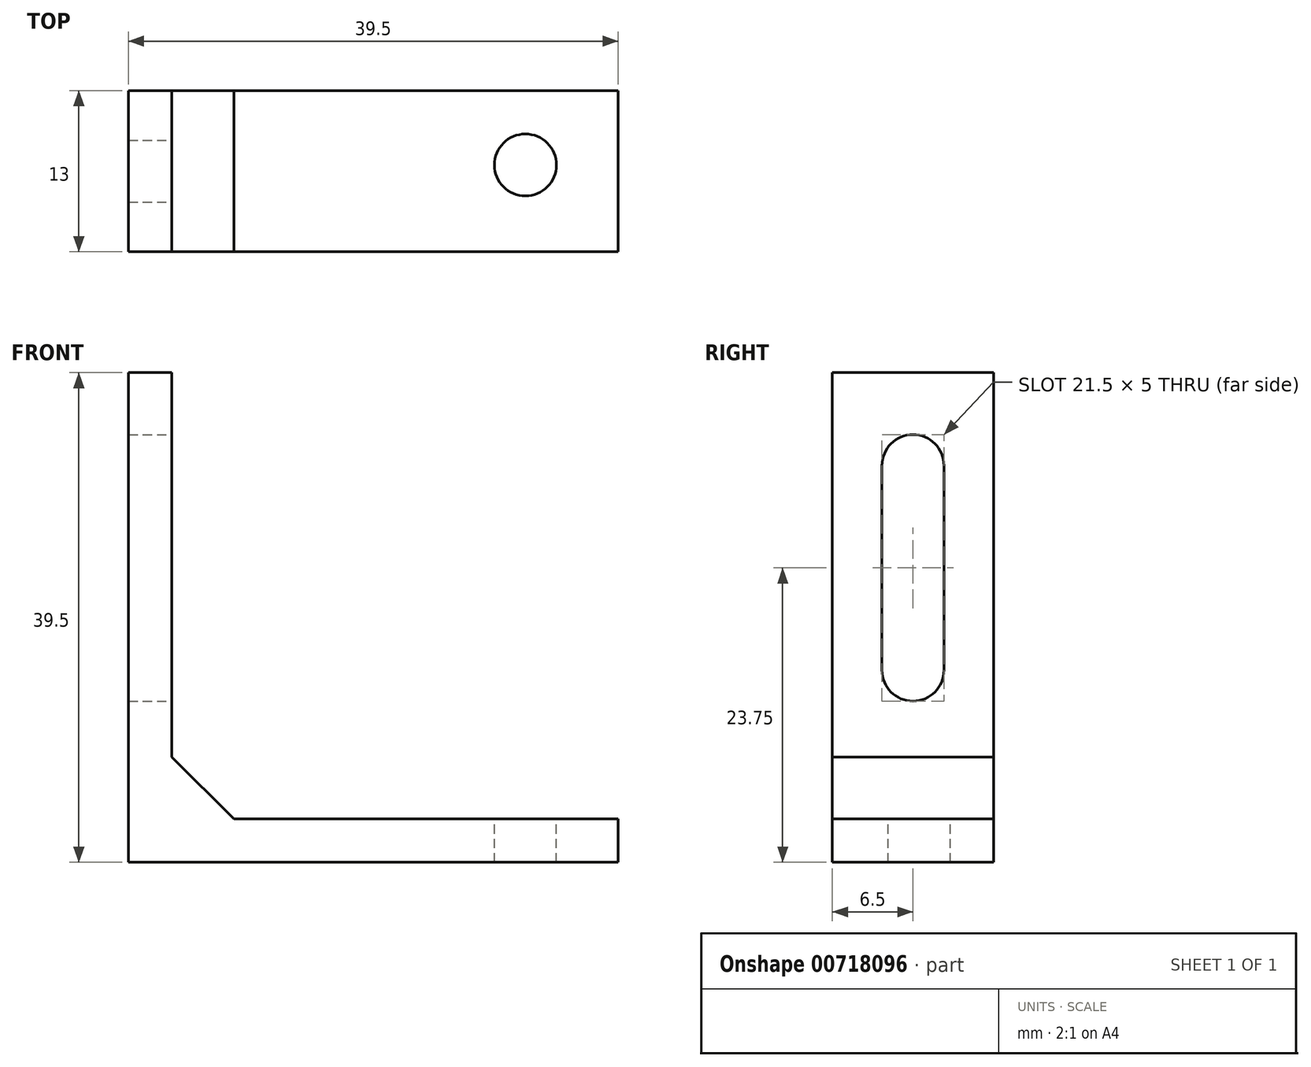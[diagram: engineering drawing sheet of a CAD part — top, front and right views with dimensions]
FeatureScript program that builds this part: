
annotation { "Feature Type Name" : "Feature", "Feature Type Description" : "" }
export const myFeature = defineFeature(function(context is Context, id is Id, definition is map)
    precondition{}
    {
        {
            var Q0;
            Q0=qCreatedBy(makeId("Front.planeOp"),FACE);
            var sketch = newSketch(context, id + "F0", { "sketchPlane" : qUnion([Q0])});
            skLineSegment(sketch, "E0", {"start": v(0, 0) * mm, "end": v(-36, 0) * mm});
            skLineSegment(sketch, "E1", {"start": v(-36, 0) * mm, "end": v(-36, 36) * mm});
            skLineSegment(sketch, "E2", {"start": v(-36, 36) * mm, "end": v(-39.5, 36) * mm});
            skLineSegment(sketch, "E3", {"start": v(-39.5, 36) * mm, "end": v(-39.5, -3.5) * mm});
            skLineSegment(sketch, "E4", {"start": v(-39.5, -3.5) * mm, "end": v(0, -3.5) * mm});
            skLineSegment(sketch, "E5", {"start": v(0, -3.5) * mm, "end": v(0, 0) * mm});
            skSolve(sketch);
        }
        {
            var Q0;
            Q0=makeQuery(id+"F0.imprint","IMPRINT",FACE,{"disambiguationData":[TD([[makeQuery(id+"F0.imprint","IMPRINT",EDGE,{"derivedFrom":sQuery(id+"F0.wireOp",EDGE,"E0")}),1.0]])]});
            extrude(context, id + "F1", {"entities" : qUnion([Q0]), "depth" : 13 * mm, "offsetDistance" : 25 * mm});
        }
        {
            var Q0;
            Q0=makeQuery(id+"F1.opExtrude","SWEPT_FACE",FACE,{"disambiguationData":[OSD([sQuery(id+"F0.wireOp",EDGE,"E1")])]});
            var sketch = newSketch(context, id + "F2", { "sketchPlane" : qUnion([Q0])});
            skCircle(sketch, "E6", {"center": v(-6.5, 28.5) * mm, "radius": 2.5 * mm});
            skCircle(sketch, "E7", {"center": v(-6.5, 12) * mm, "radius": 2.5 * mm});
            skLineSegment(sketch, "E8", {"start": v(-9, 12) * mm, "end": v(-9, 28.5) * mm});
            skLineSegment(sketch, "E9", {"start": v(-4, 28.5) * mm, "end": v(-4, 12) * mm});
            skSolve(sketch);
        }
        {
            var Q0;
            {var subQ0=sQuery(id+"F2.wireOp",EDGE,"E6");var subQ1=makeQuery(id+"F2.imprint","INTERSECT",VERTEX,{"derivedFrom":[subQ0,sQuery(id+"F2.wireOp",EDGE,"E8")]});Q0=makeQuery(id+"F2.imprint","IMPRINT",FACE,{"disambiguationData":[TD([[makeQuery(id+"F2.imprint","IMPRINT",EDGE,{"disambiguationData":[TD([[subQ1,1.0]])],"derivedFrom":subQ0}),1.0]])]});}
            var Q1;
            {var subQ0=sQuery(id+"F2.wireOp",EDGE,"E8");Q1=makeQuery(id+"F2.imprint","IMPRINT",FACE,{"disambiguationData":[TD([[makeQuery(id+"F2.imprint","IMPRINT",EDGE,{"derivedFrom":subQ0}),-1.0]])]});}
            var Q2;
            {var subQ0=sQuery(id+"F2.wireOp",EDGE,"E7");var subQ1=makeQuery(id+"F2.imprint","INTERSECT",VERTEX,{"derivedFrom":[subQ0,sQuery(id+"F2.wireOp",EDGE,"E8")]});Q2=makeQuery(id+"F2.imprint","IMPRINT",FACE,{"disambiguationData":[TD([[makeQuery(id+"F2.imprint","IMPRINT",EDGE,{"disambiguationData":[TD([[subQ1,1.0]])],"derivedFrom":subQ0}),1.0]])]});}
            extrude(context, id + "F3", {"entities" : qUnion([Q0, Q1, Q2]), "operationType" : NewBodyOperationType.REMOVE, "oppositeDirection" : true, "depth" : 25 * mm, "offsetDistance" : 25 * mm});
        }
        {
            var Q0;
            Q0=makeQuery(id+"F1.opExtrude","SWEPT_FACE",FACE,{"disambiguationData":[OSD([sQuery(id+"F0.wireOp",EDGE,"E0")])]});
            var sketch = newSketch(context, id + "F4", { "sketchPlane" : qUnion([Q0])});
            skCircle(sketch, "E10", {"center": v(-7.48, -6) * mm, "radius": 2.5 * mm});
            skSolve(sketch);
        }
        {
            var Q0;
            Q0 = qSketchRegion(id + "F4", true);
            extrude(context, id + "F5", {"entities" : qUnion([Q0]), "operationType" : NewBodyOperationType.REMOVE, "oppositeDirection" : true, "depth" : 25 * mm, "offsetDistance" : 25 * mm});
        }
        {
            var Q0;
            Q0=makeQuery(id+"F1.opExtrude","SWEPT_EDGE",EDGE,{"disambiguationData":[OSD([sQuery(id+"F0.wireOp",EDGE,"E0"),sQuery(id+"F0.wireOp",EDGE,"E1")])]});
            chamfer(context, id + "F6", {"entities" : qUnion([Q0]), "width" : 5 * mm, "tangentPropagation" : true});
        }
    });
